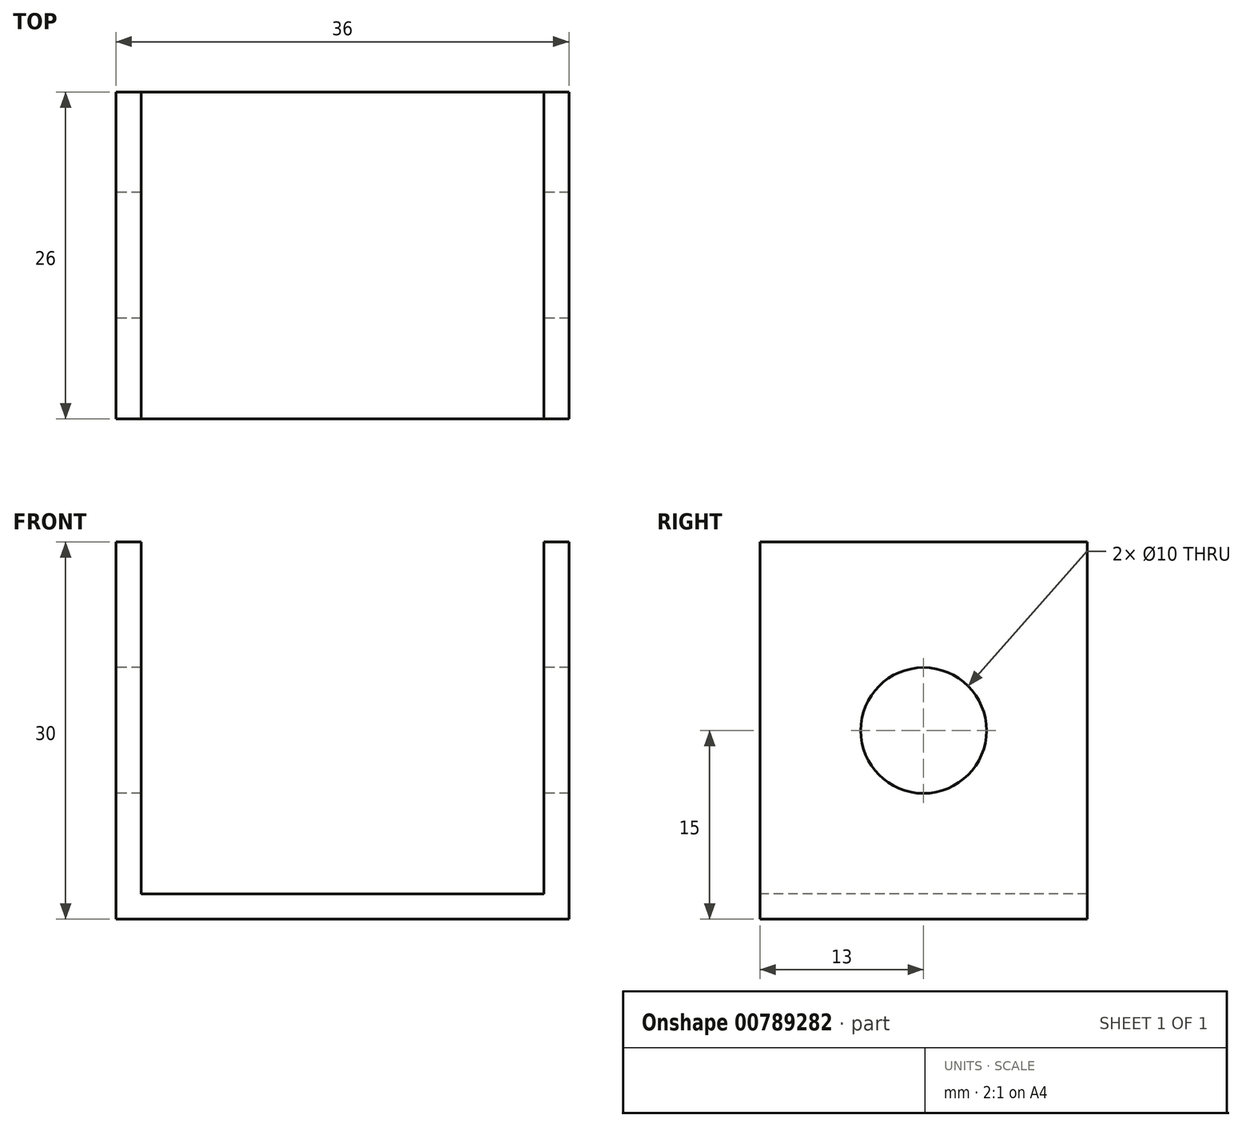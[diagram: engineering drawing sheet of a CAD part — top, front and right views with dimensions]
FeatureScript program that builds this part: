
annotation { "Feature Type Name" : "Feature", "Feature Type Description" : "" }
export const myFeature = defineFeature(function(context is Context, id is Id, definition is map)
    precondition{}
    {
        {
            var Q0;
            Q0=qCreatedBy(makeId("Top.planeOp"),FACE);
            var sketch = newSketch(context, id + "F0", { "sketchPlane" : qUnion([Q0])});
            skLineSegment(sketch, "E0.bottom", {"start": v(-18, 13) * mm, "end": v(18, 13) * mm});
            skLineSegment(sketch, "E0.top", {"start": v(-18, -13) * mm, "end": v(18, -13) * mm});
            skLineSegment(sketch, "E0.left", {"start": v(-18, 13) * mm, "end": v(-18, -13) * mm});
            skLineSegment(sketch, "E0.right", {"start": v(18, 13) * mm, "end": v(18, -13) * mm});
            skPoint(sketch, "E0.middle", {"position": v(0, 0) * mm});
            skSolve(sketch);
        }
        {
            var Q0;
            Q0=makeQuery(id+"F0.imprint","IMPRINT",FACE,{"disambiguationData":[TD([[makeQuery(id+"F0.imprint","IMPRINT",EDGE,{"derivedFrom":sQuery(id+"F0.wireOp",EDGE,"E0.bottom")}),-1.0]])]});
            extrude(context, id + "F1", {"entities" : qUnion([Q0]), "depth" : 2 * mm, "offsetDistance" : 25 * mm});
        }
        {
            var Q0;
            Q0=makeQuery(id+"F1.opExtrude","CAP_FACE",FACE,{"disambiguationData":[OSD([sQuery(id+"F0.wireOp",EDGE,"E0.bottom"),sQuery(id+"F0.wireOp",EDGE,"E0.top"),sQuery(id+"F0.wireOp",EDGE,"E0.left"),sQuery(id+"F0.wireOp",EDGE,"E0.right")])],"isStart":false});
            var sketch = newSketch(context, id + "F2", { "sketchPlane" : qUnion([Q0])});
            skLineSegment(sketch, "E1.bottom", {"start": v(-18, 13) * mm, "end": v(-16, 13) * mm});
            skLineSegment(sketch, "E1.top", {"start": v(-18, -13) * mm, "end": v(-16, -13) * mm});
            skLineSegment(sketch, "E1.left", {"start": v(-18, 13) * mm, "end": v(-18, -13) * mm});
            skLineSegment(sketch, "E1.right", {"start": v(-16, 13) * mm, "end": v(-16, -13) * mm});
            skLineSegment(sketch, "E2.bottom", {"start": v(18, 13) * mm, "end": v(16, 13) * mm});
            skLineSegment(sketch, "E2.top", {"start": v(18, -13) * mm, "end": v(16, -13) * mm});
            skLineSegment(sketch, "E2.left", {"start": v(18, 13) * mm, "end": v(18, -13) * mm});
            skLineSegment(sketch, "E2.right", {"start": v(16, 13) * mm, "end": v(16, -13) * mm});
            skSolve(sketch);
        }
        {
            var Q0;
            Q0=makeQuery(id+"F2.imprint","IMPRINT",FACE,{"disambiguationData":[TD([[makeQuery(id+"F2.imprint","IMPRINT",EDGE,{"derivedFrom":sQuery(id+"F2.wireOp",EDGE,"E2.bottom")}),-1.0]])]});
            var Q1;
            Q1=makeQuery(id+"F2.imprint","IMPRINT",FACE,{"disambiguationData":[TD([[makeQuery(id+"F2.imprint","IMPRINT",EDGE,{"derivedFrom":sQuery(id+"F2.wireOp",EDGE,"E1.bottom")}),-1.0]])]});
            extrude(context, id + "F3", {"entities" : qUnion([Q0, Q1]), "operationType" : NewBodyOperationType.ADD, "depth" : 28 * mm, "offsetDistance" : 25 * mm});
        }
        {
            var Q0;
            Q0=makeQuery(id+"F3.boolean.opBoolean","MERGE",FACE,{"derivedFrom":[makeQuery(id+"F1.opExtrude","SWEPT_FACE",FACE,{"disambiguationData":[OSD([sQuery(id+"F0.wireOp",EDGE,"E0.left")])]}),makeQuery(id+"F3.opExtrude","SWEPT_FACE",FACE,{"disambiguationData":[OSD([sQuery(id+"F2.wireOp",EDGE,"E1.left")])]})]});
            var sketch = newSketch(context, id + "F4", { "sketchPlane" : qUnion([Q0])});
            skCircle(sketch, "E3", {"center": v(0, 15) * mm, "radius": 5 * mm});
            skSolve(sketch);
        }
        {
            var Q0;
            Q0=makeQuery(id+"F4.imprint","IMPRINT",FACE,{"disambiguationData":[TD([[makeQuery(id+"F4.imprint","IMPRINT",EDGE,{"derivedFrom":sQuery(id+"F4.wireOp",EDGE,"E3")}),1.0]])]});
            extrude(context, id + "F5", {"entities" : qUnion([Q0]), "operationType" : NewBodyOperationType.REMOVE, "oppositeDirection" : true, "depth" : 265 * mm, "offsetDistance" : 25 * mm});
        }
    });
